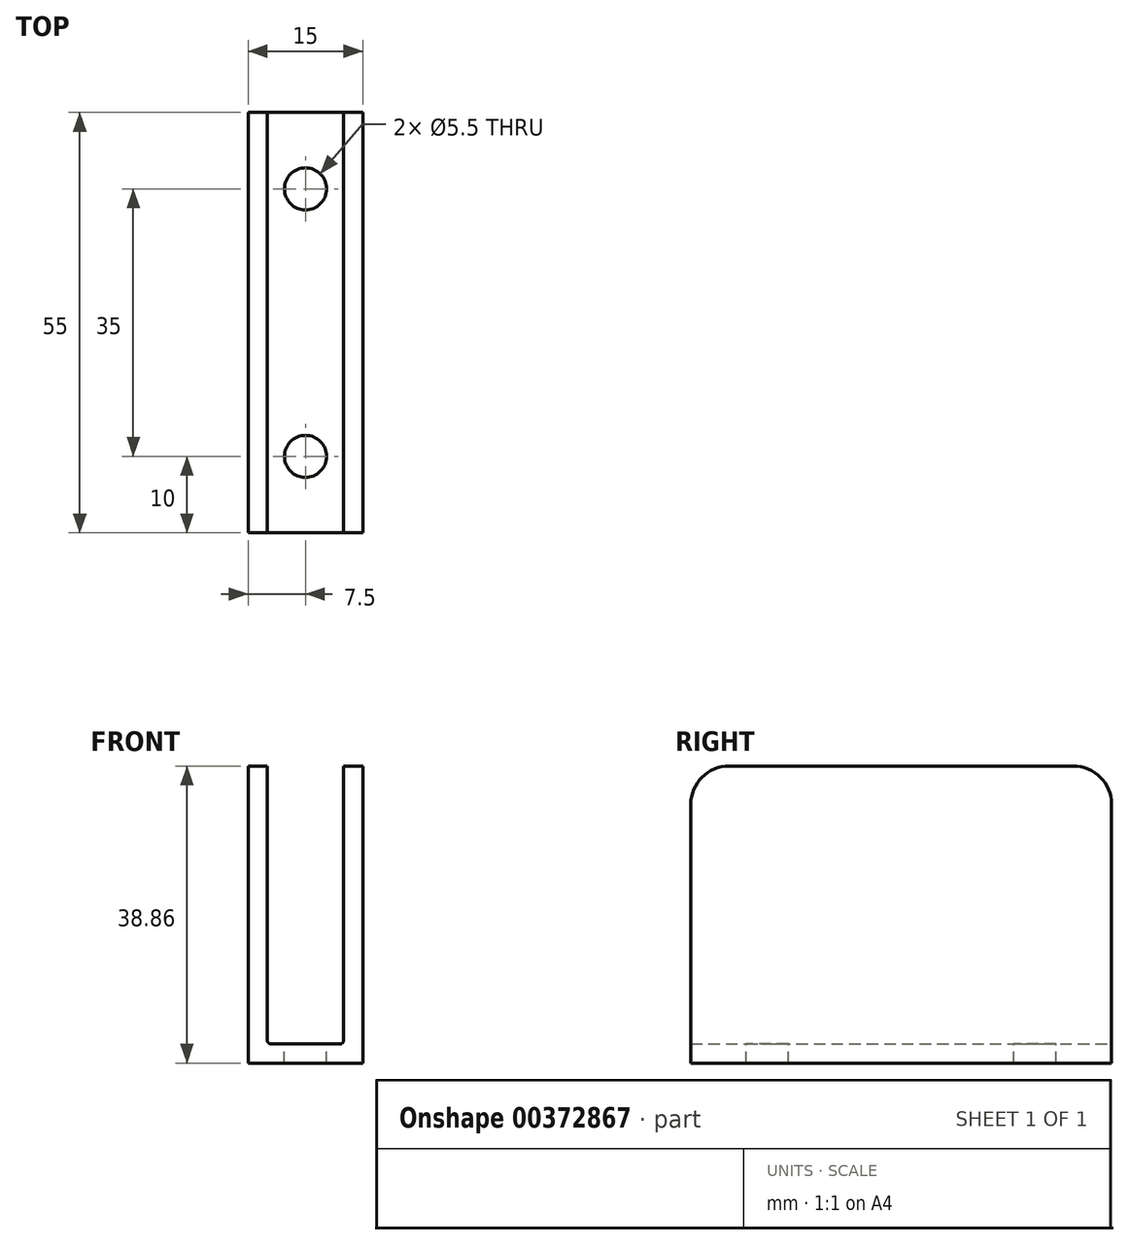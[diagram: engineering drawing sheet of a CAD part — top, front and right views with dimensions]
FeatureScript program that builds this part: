
annotation { "Feature Type Name" : "Feature", "Feature Type Description" : "" }
export const myFeature = defineFeature(function(context is Context, id is Id, definition is map)
    precondition{}
    {
        {
            var Q0;
            Q0=qCreatedBy(makeId("Front.planeOp"),FACE);
            var sketch = newSketch(context, id + "F0", { "sketchPlane" : qUnion([Q0])});
            skLineSegment(sketch, "E0", {"start": v(0, 0) * mm, "end": v(-7.5, 0) * mm});
            skLineSegment(sketch, "E1", {"start": v(-7.5, 0) * mm, "end": v(-7.5, 38.86) * mm});
            skLineSegment(sketch, "E2", {"start": v(0, 43.2) * mm, "end": v(0, -29.2) * mm, "construction": true});
            skLineSegment(sketch, "E3.MirrorCS", {"start": v(7.5, 0) * mm, "end": v(7.5, 38.86) * mm});
            skLineSegment(sketch, "E4.MirrorCS", {"start": v(0, 0) * mm, "end": v(7.5, 0) * mm});
            skLineSegment(sketch, "E5", {"start": v(-7.5, 38.86) * mm, "end": v(-5, 38.86) * mm});
            skLineSegment(sketch, "E6", {"start": v(-5, 38.86) * mm, "end": v(-5, 2.5) * mm});
            skLineSegment(sketch, "E7", {"start": v(-5, 2.5) * mm, "end": v(5, 2.5) * mm});
            skLineSegment(sketch, "E8", {"start": v(5, 2.5) * mm, "end": v(5, 38.86) * mm});
            skLineSegment(sketch, "E9", {"start": v(5, 38.86) * mm, "end": v(7.5, 38.86) * mm});
            skSolve(sketch);
        }
        {
            var Q0;
            Q0=makeQuery(id+"F0.imprint","IMPRINT",FACE,{"disambiguationData":[TD([[makeQuery(id+"F0.imprint","IMPRINT",EDGE,{"derivedFrom":sQuery(id+"F0.wireOp",EDGE,"E0")}),-1.0]])]});
            extrude(context, id + "F1", {"entities" : qUnion([Q0]), "endBound" : BoundingType.SYMMETRIC, "depth" : 55 * mm});
        }
        {
            var Q0;
            Q0=makeQuery(id+"F1.opExtrude","CAP_EDGE",EDGE,{"disambiguationData":[OSD([sQuery(id+"F0.wireOp",EDGE,"E9")])],"isStart":false});
            var Q1;
            Q1=makeQuery(id+"F1.opExtrude","CAP_EDGE",EDGE,{"disambiguationData":[OSD([sQuery(id+"F0.wireOp",EDGE,"E5")])],"isStart":false});
            var Q2;
            Q2=makeQuery(id+"F1.opExtrude","CAP_EDGE",EDGE,{"disambiguationData":[OSD([sQuery(id+"F0.wireOp",EDGE,"E9")])],"isStart":true});
            var Q3;
            Q3=makeQuery(id+"F1.opExtrude","CAP_EDGE",EDGE,{"disambiguationData":[OSD([sQuery(id+"F0.wireOp",EDGE,"E5")])],"isStart":true});
            fillet(context, id + "F2", {"entities" : qUnion([Q0, Q1, Q2, Q3]), "radius" : 5 * mm, "tangentPropagation" : true, "allowEdgeOverflow" : false});
        }
        {
            var Q0;
            Q0=makeQuery(id+"F1.opExtrude","SWEPT_EDGE",EDGE,{"disambiguationData":[OSD([sQuery(id+"F0.wireOp",EDGE,"E6"),sQuery(id+"F0.wireOp",EDGE,"E7")])]});
            var Q1;
            Q1=makeQuery(id+"F1.opExtrude","SWEPT_EDGE",EDGE,{"disambiguationData":[OSD([sQuery(id+"F0.wireOp",EDGE,"E7"),sQuery(id+"F0.wireOp",EDGE,"E8")])]});
            fillet(context, id + "F3", {"entities" : qUnion([Q0, Q1]), "radius" : 0.5 * mm, "tangentPropagation" : true, "allowEdgeOverflow" : false});
        }
        {
            var Q0;
            Q0=makeQuery(id+"F1.opExtrude","SWEPT_FACE",FACE,{"disambiguationData":[OSD([sQuery(id+"F0.wireOp",EDGE,"E7")])]});
            var sketch = newSketch(context, id + "F4", { "sketchPlane" : qUnion([Q0])});
            skPoint(sketch, "E10", {"position": v(0, 17.5) * mm});
            skPoint(sketch, "E11", {"position": v(0, -17.5) * mm});
            skSolve(sketch);
        }
        {
            var Q0;
            Q0=sQuery(id+"F4.wireOp",VERTEX,"E10");
            var Q1;
            Q1=sQuery(id+"F4.wireOp",VERTEX,"E11");
            var Q2;
            Q2=makeQuery(id+"F1.opExtrude","SWEPT_BODY",BODY,{"disambiguationData":[OSD([sQuery(id+"F0.wireOp",EDGE,"E0"),sQuery(id+"F0.wireOp",EDGE,"E1"),sQuery(id+"F0.wireOp",EDGE,"E3.MirrorCS"),sQuery(id+"F0.wireOp",EDGE,"E4.MirrorCS"),sQuery(id+"F0.wireOp",EDGE,"E5"),sQuery(id+"F0.wireOp",EDGE,"E6"),sQuery(id+"F0.wireOp",EDGE,"E7"),sQuery(id+"F0.wireOp",EDGE,"E8"),sQuery(id+"F0.wireOp",EDGE,"E9")])]});
            hole(context, id + "F5", {"style" : HoleStyle.SIMPLE, "endStyle" : HoleEndStyle.THROUGH, "standardTappedOrClearance" : lookupTablePath({ "standard" : "ISO", "size" : "5.5", "type" : "Drilled" }), "standardBlindInLast" : lookupTablePath({ "standard" : "ISO", "size" : "5.5", "type" : "Drilled" }), "holeDiameter" : 5.5 * mm, "isTappedThrough" : true, "tappedDepth" : 12 * mm, "tapClearance" : 3, "locations" : qUnion([Q0, Q1]), "scope" : qUnion([Q2])});
        }
    });
